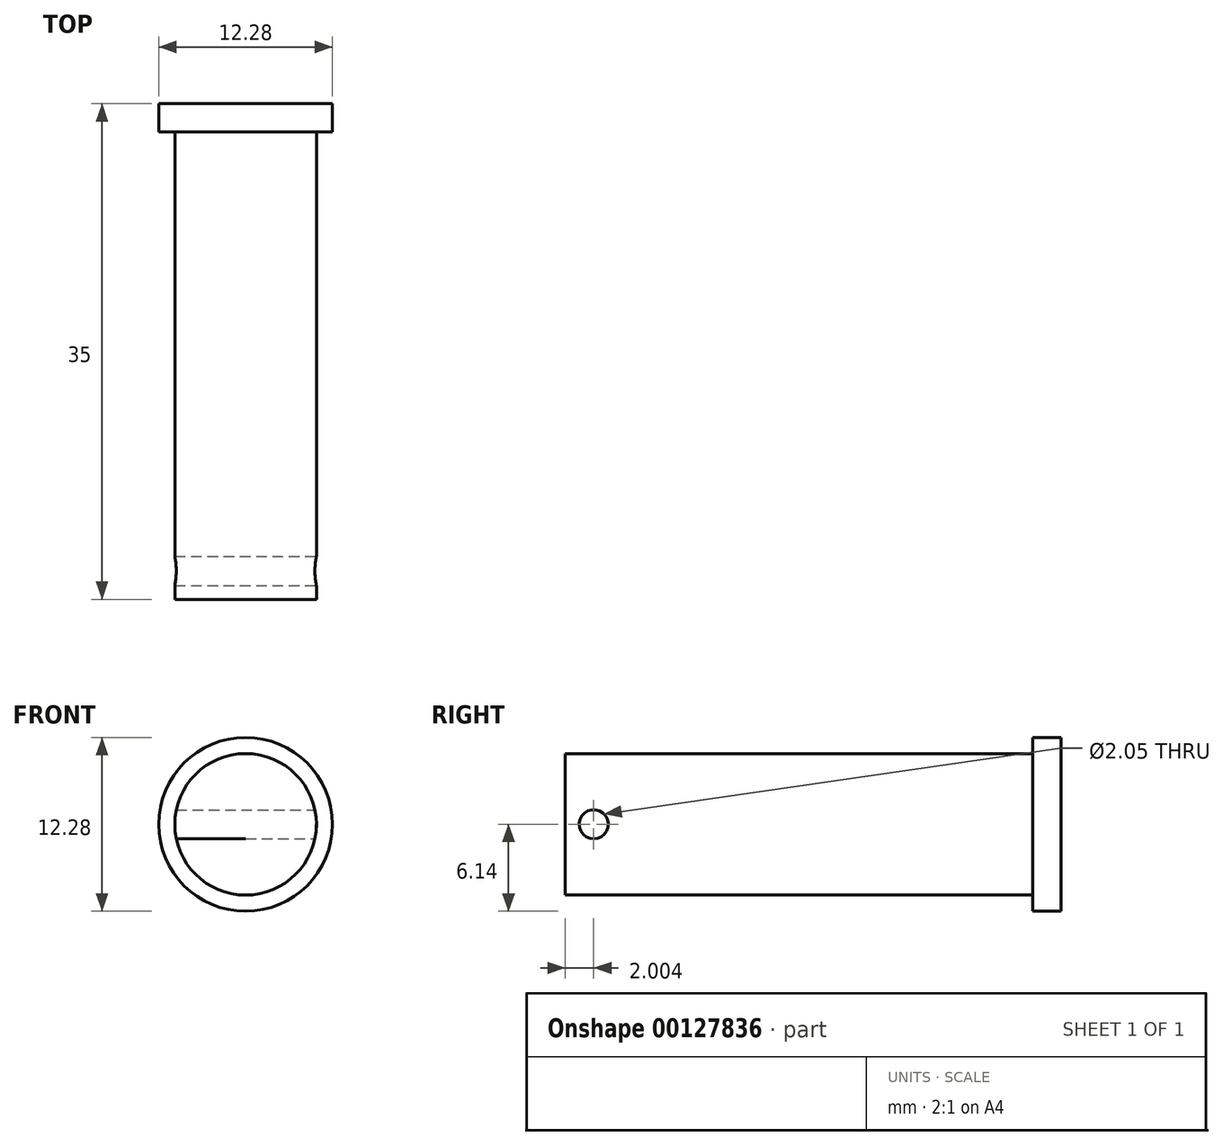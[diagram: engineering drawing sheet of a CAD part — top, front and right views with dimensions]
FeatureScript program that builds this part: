
annotation { "Feature Type Name" : "Feature", "Feature Type Description" : "" }
export const myFeature = defineFeature(function(context is Context, id is Id, definition is map)
    precondition{}
    {
        {
            var Q0;
            Q0=qCreatedBy(makeId("Front.planeOp"),FACE);
            var sketch = newSketch(context, id + "F0", { "sketchPlane" : qUnion([Q0])});
            skCircle(sketch, "E0", {"center": v(0, 0) * mm, "radius": 6.13 * mm});
            skSolve(sketch);
        }
        {
            var Q0;
            Q0 = qSketchRegion(id + "F0", true);
            extrude(context, id + "F1", {"entities" : qUnion([Q0]), "depth" : 2 * mm});
        }
        {
            var Q0;
            Q0=makeQuery(id+"F1.opExtrude","CAP_FACE",FACE,{"disambiguationData":[OSD([sQuery(id+"F0.wireOp",EDGE,"E0")])],"isStart":false});
            var sketch = newSketch(context, id + "F2", { "sketchPlane" : qUnion([Q0])});
            skCircle(sketch, "E1", {"center": v(0, 0) * mm, "radius": 5 * mm});
            skSolve(sketch);
        }
        {
            var Q0;
            Q0 = qSketchRegion(id + "F2", true);
            extrude(context, id + "F3", {"entities" : qUnion([Q0]), "operationType" : NewBodyOperationType.ADD, "depth" : 33 * mm});
        }
        {
            var Q0;
            Q0=qCreatedBy(makeId("Right.planeOp"),FACE);
            cPlane(context, id + "F4", {"entities" : qUnion([Q0]), "cplaneType" : CPlaneType.OFFSET, "offset" : 5 * mm, "width" : 150 * mm, "height" : 150 * mm});
        }
        {
            var Q0;
            Q0=qCreatedBy(id+"F4.planeOp",FACE);
            var sketch = newSketch(context, id + "F5", { "sketchPlane" : qUnion([Q0])});
            skCircle(sketch, "E2", {"center": v(-33, 0) * mm, "radius": 1.02 * mm});
            skSolve(sketch);
        }
        {
            var Q0;
            Q0 = qSketchRegion(id + "F5", true);
            extrude(context, id + "F6", {"entities" : qUnion([Q0]), "operationType" : NewBodyOperationType.REMOVE, "endBound" : BoundingType.THROUGH_ALL, "oppositeDirection" : true, "depth" : 25 * mm});
        }
    });
